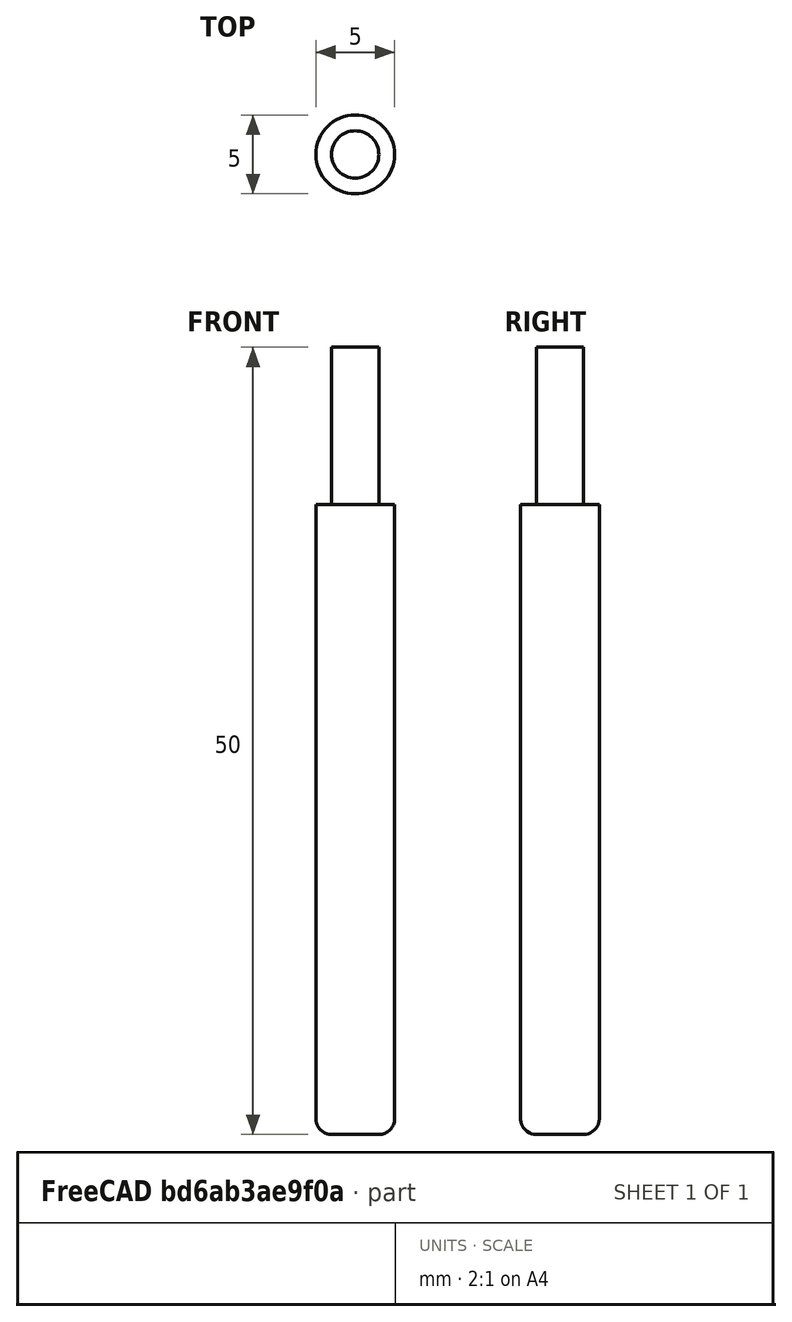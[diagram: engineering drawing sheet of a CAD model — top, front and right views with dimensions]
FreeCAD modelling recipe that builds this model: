
FCSTD DOCUMENT  (FreeCAD 0.21R32460 (Git))
Label: bullnose
License: Creative Commons Attribution 4.0
LicenseURL: https://creativecommons.org/licenses/by/4.0/
objects: Sketcher::SketchObject×1, PartDesign::Revolution×1, App::FeaturePython×1, PartDesign::Body×1
note: 4 computed .brp shape members not serialized (recipe doc carries the construction recipe); baked Part::Feature solids carry a one-line shape summary decoded from their .brp

FEATURE [Sketcher::SketchObject] Sketch
  FullyConstrained = true
  MapMode = 5
  Placement = pos=(0,0,0) rot=(1,0,0;1.5708rad)
  Support = -> [XZ_Plane]
  expr: Constraints[12] = <<Attributes>>.ShankDiameter
  expr: Constraints[19] = <<Attributes>>.FlatRadius
  expr: Constraints[20] = <<Attributes>>.CuttingEdgeHeight
  expr: Constraints[5] = <<Attributes>>.Diameter
  expr: Constraints[6] = <<Attributes>>.Length
  sketch-geometry (9):
    g0: LineSegment StartX=0 StartY=50 StartZ=0 EndX=0 EndY=0 EndZ=0
    g1: LineSegment StartX=0 StartY=0 StartZ=0 EndX=1.5 EndY=0 EndZ=0
    g2: LineSegment StartX=2.5 StartY=1 StartZ=0 EndX=2.5 EndY=40 EndZ=0
    g3: LineSegment StartX=1.5 StartY=50 StartZ=0 EndX=0 EndY=50 EndZ=0
    g4: LineSegment StartX=2.5 StartY=0 StartZ=0 EndX=-2.5 EndY=0 EndZ=0
    g5: LineSegment StartX=1.5 StartY=40.01 StartZ=0 EndX=2.5 EndY=40 EndZ=0
    g6: LineSegment StartX=1.5 StartY=50 StartZ=0 EndX=1.5 EndY=40.01 EndZ=0
    g7: LineSegment StartX=-1.5 StartY=50 StartZ=0 EndX=1.5 EndY=50 EndZ=0
    g8: ArcOfCircle CenterX=1.5 CenterY=1 CenterZ=0 NormalX=0 NormalY=0 NormalZ=1 AngleXU=0 Radius=1 StartAngle=4.71239 EndAngle=6.28319
  constraints (24):
    c: Vertical(g0)
    c: Coincident(g0,g1)
    c: Horizontal(g1)
    c: Vertical(g2)
    c: Horizontal(g3)
    c: DistanceX(g4,g4) = 5
    c: DistanceY(g4,g3) = 50
    c: Coincident(g2,g5)
    c: Vertical(g6)
    c: Coincident(g3,g6)
    c: Symmetric(g7,g7,g0)
    c: Coincident(g7,g3)
    c: DistanceX(g7,g7) = 3
    c: Coincident(g5,g6)
    c: Tangent(g1,g8) = -1.5708
    c: Tangent(g2,g8) = -1.5708
    c: PointOnObject(g0,g4)
    c: Symmetric(g4,g4,g-2)
    c: Vertical(g4,g2)
    c: DistanceX(g1,g1) = 1.5
    c: DistanceY(g1,g2) = 40
    c: Coincident(g0,g3)
    c: Coincident(g-1,g0)
    c: DistanceY(g2,g5) = 0.01
FEATURE [PartDesign::Revolution] Revolution
  AllowMultiFace = false
  Angle = 360
  Axis = (0,-2e-16,1)
  Base = (0,0,0)
  Placement = pos=(0,0,0) rot=(1,0,0;1.5708rad)
  Profile = -> Sketch
  ReferenceAxis = -> Sketch [V_Axis]
  Reversed = true
FEATURE [App::FeaturePython] PropertyBag  label="Attributes"  # WARN: FeaturePython — macro-defined, semantics opaque (R4)
  Chipload = 0
  CustomPropertyGroups = Attributes | Shape
  CuttingEdgeHeight = 40
  Diameter = 5
  FlatRadius = 1.5
  Flutes = 0
  Length = 50
  Material = 0
  ShankDiameter = 3
FEATURE [PartDesign::Body] Body  label="Bullnose"
  Group = -> [Sketch,Revolution,PropertyBag]
  Origin = -> Origin
  Tip = -> Revolution
